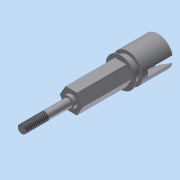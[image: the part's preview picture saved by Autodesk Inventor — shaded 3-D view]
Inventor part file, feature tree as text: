
AUTODESK INVENTOR PART (.ipt)
format: ipt  version: 2011 SP1 (Build 150282100, 282)  size: 155,648 bytes
history: native  units: in
note: dims shown in document units (in); Inventor stores cm internally (conversion verified against a paired STEP export)
features: sketch x9, extrude x8, projected_geometry x2, thread x1, revolve x1
ambient origin geometry x8: Origin, YZ Plane, XZ Plane, XY Plane, X Axis, Y Axis, Z Axis, Center Point
bodies: Solid1 (feature_tree)
feature tree (21):
  extrude  "Extrusion1"  Depth=0.75in TaperAngle=0.0deg
  extrude  "Extrusion2"  Depth=0.05in TaperAngle=0.0deg
  extrude  "Extrusion3"  Depth=0.7in TaperAngle=0.0deg
  thread  "Thread1"  [1 undecoded]
  extrude  "Extrusion4"  Depth=0.01in TaperAngle=0.0deg
  extrude  "Extrusion5"  Depth=0.1in TaperAngle=0.0deg
  extrude  "Extrusion6"  Depth=0.08in TaperAngle=0.0deg
  extrude  "Extrusion8"  Depth=0.25in TaperAngle=0.0deg
  revolve  "Revolution1"  Angle=90.0deg
  extrude  "Extrusion9"  Depth=0.25in TaperAngle=0.0deg
  sketch  "Sketch1"  dims[d0=0.3in d1=0.75in d2=0.0in]
  sketch  "Sketch2"  dims[d3=0.18in d4=0.05in d5=0.0in]
  sketch  "Sketch3"  dims[d6=0.125in d7=0.7in d8=0.0in d9=0.35in d10=0.0in]
  sketch  "Sketch4"  dims[d11=0.45in d12=0.01in d13=0.0in]
  sketch  "Sketch5"  dims[d14=0.35in d15=0.1in d16=0.0in]
  sketch  "Sketch6"  dims[d17=0.45in d18=0.08in d19=0.0in]
  sketch  "Sketch7"  dims[d20=0.3in d30=0.25in d31=0.0in]
  sketch  "Sketch13"  dims[d32=30.0deg d33=90.0deg]
  sketch  "Sketch16"  dims[d45=0.7874in d47=360.0deg d49=0.25in d50=0.0in]
  projected_geometry  "Project Cut Edges1"
  projected_geometry  "Project Cut Edges2"
note: 1 required parameter value undecoded (feature->parameter linkage not recoverable at this tier; creation-order binding heuristic only, values carry confidence <= 0.55)
